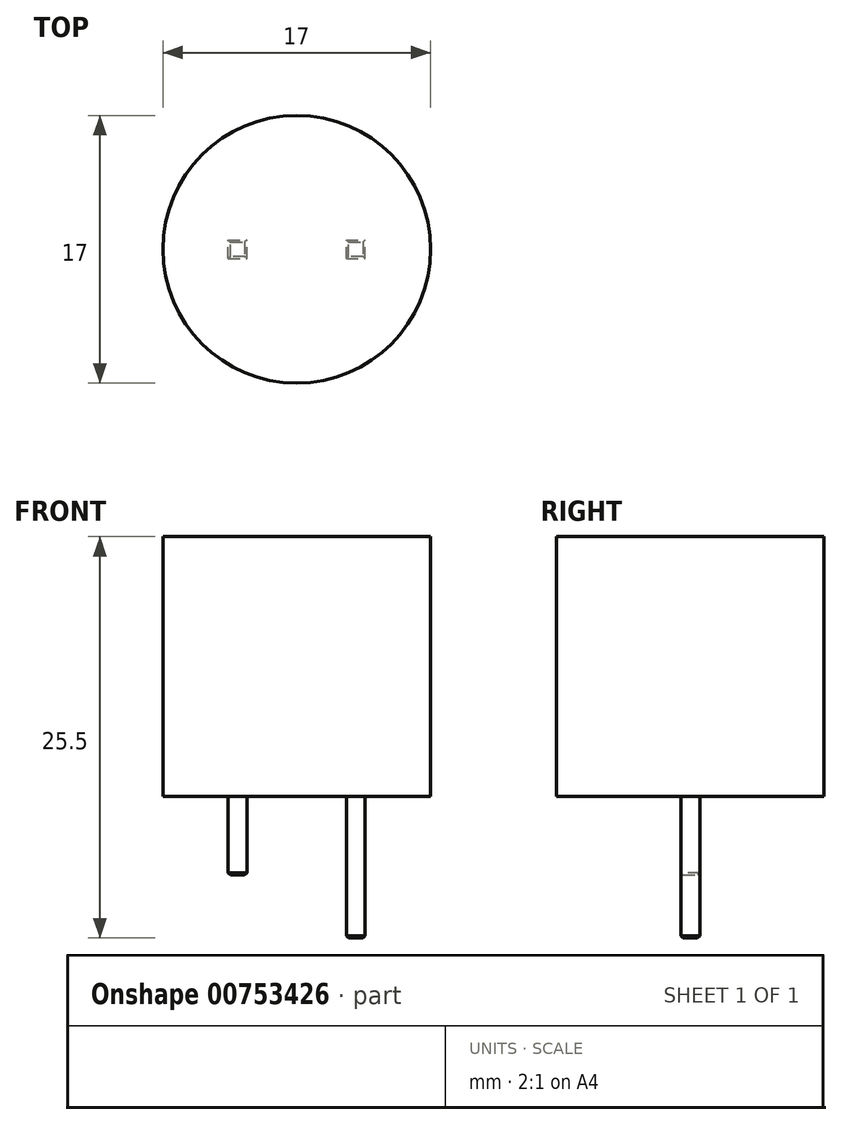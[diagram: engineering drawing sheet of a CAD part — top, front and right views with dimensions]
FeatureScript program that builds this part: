
annotation { "Feature Type Name" : "Feature", "Feature Type Description" : "" }
export const myFeature = defineFeature(function(context is Context, id is Id, definition is map)
    precondition{}
    {
        {
            var Q0;
            Q0=qCreatedBy(makeId("Top.planeOp"),FACE);
            var sketch = newSketch(context, id + "F0", { "sketchPlane" : qUnion([Q0])});
            skCircle(sketch, "E0", {"center": v(0, 0) * mm, "radius": 8.5 * mm});
            skSolve(sketch);
        }
        {
            var Q0;
            Q0=makeQuery(id+"F0.imprint","IMPRINT",FACE,{"disambiguationData":[TD([[makeQuery(id+"F0.imprint","IMPRINT",EDGE,{"derivedFrom":sQuery(id+"F0.wireOp",EDGE,"E0")}),1.0]])]});
            extrude(context, id + "F1", {"entities" : qUnion([Q0]), "depth" : 16.5 * mm, "offsetDistance" : 25 * mm});
        }
        {
            var Q0;
            Q0=makeQuery(id+"F1.opExtrude","CAP_FACE",FACE,{"disambiguationData":[OSD([sQuery(id+"F0.wireOp",EDGE,"E0")])],"isStart":true});
            var sketch = newSketch(context, id + "F2", { "sketchPlane" : qUnion([Q0])});
            skLineSegment(sketch, "E1.bottom", {"start": v(-4.35, 0.6) * mm, "end": v(-3.15, 0.6) * mm});
            skLineSegment(sketch, "E1.top", {"start": v(-4.35, -0.6) * mm, "end": v(-3.15, -0.6) * mm});
            skLineSegment(sketch, "E1.left", {"start": v(-4.35, 0.6) * mm, "end": v(-4.35, -0.6) * mm});
            skLineSegment(sketch, "E1.right", {"start": v(-3.15, 0.6) * mm, "end": v(-3.15, -0.6) * mm});
            skLineSegment(sketch, "E2.bottom", {"start": v(3.15, 0.6) * mm, "end": v(4.35, 0.6) * mm});
            skLineSegment(sketch, "E2.top", {"start": v(3.15, -0.6) * mm, "end": v(4.35, -0.6) * mm});
            skLineSegment(sketch, "E2.left", {"start": v(3.15, 0.6) * mm, "end": v(3.15, -0.6) * mm});
            skLineSegment(sketch, "E2.right", {"start": v(4.35, 0.6) * mm, "end": v(4.35, -0.6) * mm});
            skLineSegment(sketch, "E3", {"start": v(3.75, 0.6) * mm, "end": v(3.75, -0.6) * mm, "construction": true});
            skLineSegment(sketch, "E4", {"start": v(-3.75, 0.6) * mm, "end": v(-3.75, -0.6) * mm, "construction": true});
            skSolve(sketch);
        }
        {
            var Q0;
            Q0=makeQuery(id+"F2.imprint","IMPRINT",FACE,{"disambiguationData":[TD([[makeQuery(id+"F2.imprint","IMPRINT",EDGE,{"derivedFrom":sQuery(id+"F2.wireOp",EDGE,"E1.bottom")}),-1.0]])]});
            extrude(context, id + "F3", {"entities" : qUnion([Q0]), "operationType" : NewBodyOperationType.ADD, "depth" : 5 * mm, "offsetDistance" : 25 * mm});
        }
        {
            var Q0;
            Q0=makeQuery(id+"F2.imprint","IMPRINT",FACE,{"disambiguationData":[TD([[makeQuery(id+"F2.imprint","IMPRINT",EDGE,{"derivedFrom":sQuery(id+"F2.wireOp",EDGE,"E2.bottom")}),-1.0]])]});
            extrude(context, id + "F4", {"entities" : qUnion([Q0]), "operationType" : NewBodyOperationType.ADD, "depth" : 9 * mm, "offsetDistance" : 25 * mm});
        }
        {
            var Q0;
            Q0=makeQuery(id+"F3.opExtrude","CAP_EDGE",EDGE,{"disambiguationData":[OSD([sQuery(id+"F2.wireOp",EDGE,"E1.bottom")])],"isStart":false});
            var Q1;
            Q1=makeQuery(id+"F3.opExtrude","CAP_EDGE",EDGE,{"disambiguationData":[OSD([sQuery(id+"F2.wireOp",EDGE,"E1.left")])],"isStart":false});
            var Q2;
            Q2=makeQuery(id+"F3.opExtrude","CAP_EDGE",EDGE,{"disambiguationData":[OSD([sQuery(id+"F2.wireOp",EDGE,"E1.top")])],"isStart":false});
            var Q3;
            Q3=makeQuery(id+"F3.opExtrude","CAP_EDGE",EDGE,{"disambiguationData":[OSD([sQuery(id+"F2.wireOp",EDGE,"E1.right")])],"isStart":false});
            var Q4;
            Q4=makeQuery(id+"F4.opExtrude","CAP_EDGE",EDGE,{"disambiguationData":[OSD([sQuery(id+"F2.wireOp",EDGE,"E2.left")])],"isStart":false});
            var Q5;
            Q5=makeQuery(id+"F4.opExtrude","CAP_EDGE",EDGE,{"disambiguationData":[OSD([sQuery(id+"F2.wireOp",EDGE,"E2.bottom")])],"isStart":false});
            var Q6;
            Q6=makeQuery(id+"F4.opExtrude","CAP_EDGE",EDGE,{"disambiguationData":[OSD([sQuery(id+"F2.wireOp",EDGE,"E2.right")])],"isStart":false});
            var Q7;
            Q7=makeQuery(id+"F4.opExtrude","CAP_EDGE",EDGE,{"disambiguationData":[OSD([sQuery(id+"F2.wireOp",EDGE,"E2.top")])],"isStart":false});
            chamfer(context, id + "F5", {"entities" : qUnion([Q0, Q1, Q2, Q3, Q4, Q5, Q6, Q7]), "width" : 0.15 * mm, "tangentPropagation" : true});
        }
    });
